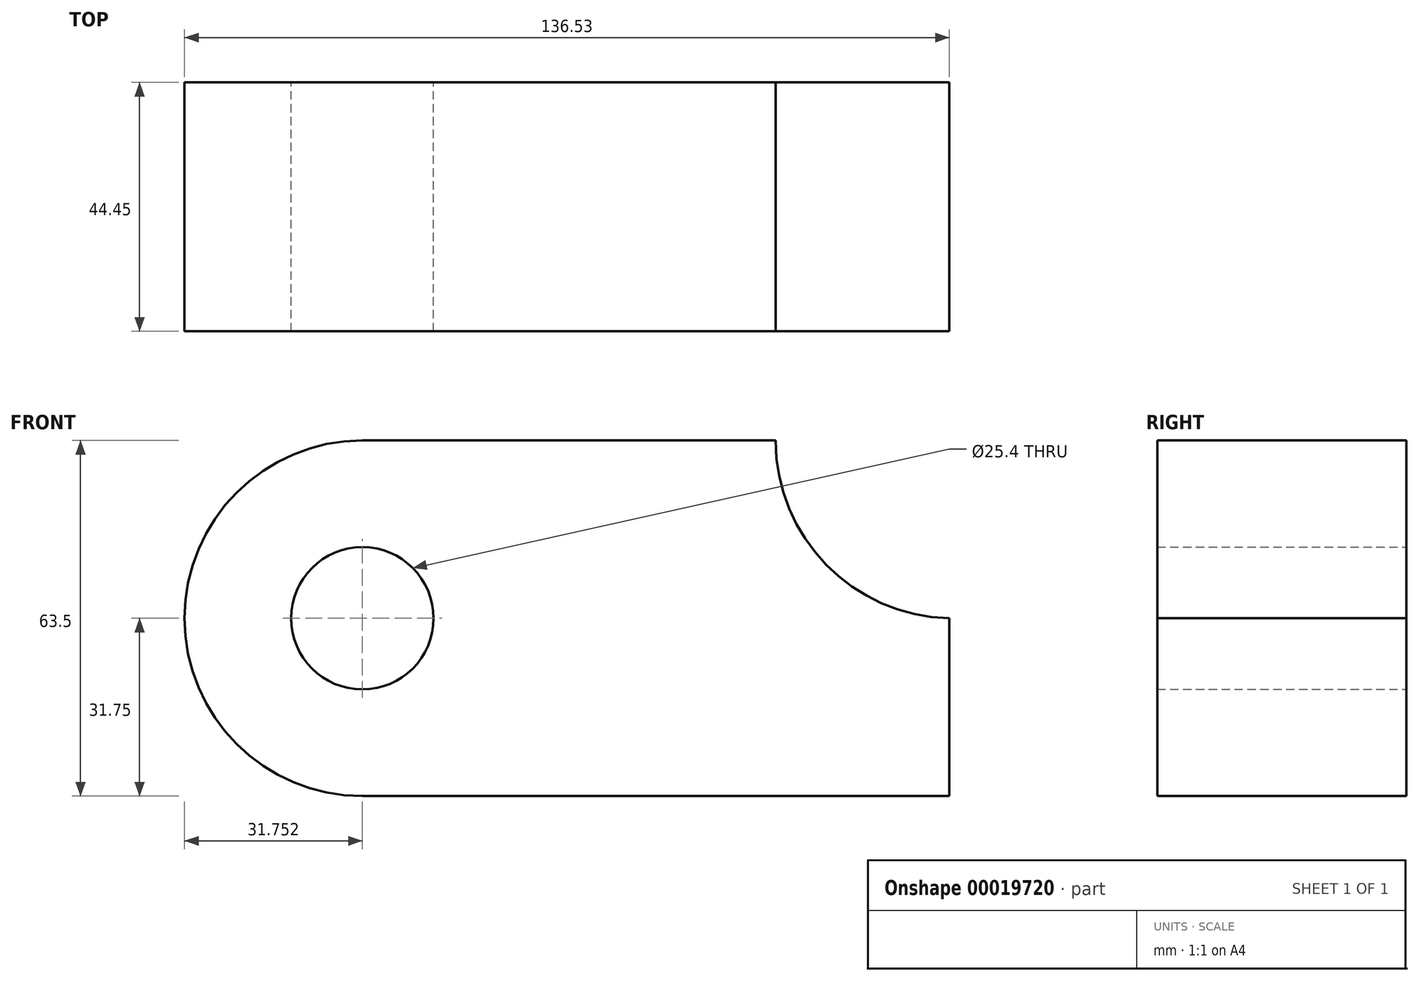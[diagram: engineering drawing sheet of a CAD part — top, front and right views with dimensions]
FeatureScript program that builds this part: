
annotation { "Feature Type Name" : "Feature", "Feature Type Description" : "" }
export const myFeature = defineFeature(function(context is Context, id is Id, definition is map)
    precondition{}
    {
        {
            var Q0;
            Q0=qCreatedBy(makeId("Front.planeOp"),FACE);
            var sketch = newSketch(context, id + "F0", { "sketchPlane" : qUnion([Q0])});
            skLineSegment(sketch, "E0.rect.bottom", {"start": v(21.38, 31.75) * mm, "end": v(-52.39, 31.75) * mm});
            skLineSegment(sketch, "E0.rect.top", {"start": v(52.39, -31.75) * mm, "end": v(-52.39, -31.75) * mm});
            skLineSegment(sketch, "E0.rect.left", {"start": v(52.39, 0) * mm, "end": v(52.39, -31.75) * mm});
            skLineSegment(sketch, "E0.rect.right", {"start": v(-52.39, 31.75) * mm, "end": v(-52.39, 12.7) * mm});
            skPoint(sketch, "E0.rect.middle", {"position": v(0, 0) * mm});
            skArc(sketch, "E1", {"start": v(21.38, 31.75) * mm, "mid": v(30.42, 9.56) * mm, "end": v(52.39, 0) * mm});
            skPoint(sketch, "E2.orphan", {"position": v(52.39, 31.75) * mm});
            skArc(sketch, "E3", {"start": v(-52.39, 31.75) * mm, "mid": v(-84.14, 0) * mm, "end": v(-52.39, -31.75) * mm});
            skCircle(sketch, "E4", {"center": v(-52.39, 0) * mm, "radius": 12.7 * mm});
            skLineSegment(sketch, "E5.trimOffspring", {"start": v(-52.39, -12.7) * mm, "end": v(-52.39, -31.75) * mm});
            skSolve(sketch);
        }
        {
            var Q0;
            Q0 = qSketchRegion(id + "F0", true);
            extrude(context, id + "F1", {"entities" : qUnion([Q0]), "depth" : 44.45 * mm});
        }
    });
